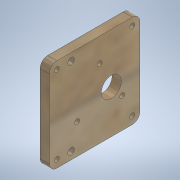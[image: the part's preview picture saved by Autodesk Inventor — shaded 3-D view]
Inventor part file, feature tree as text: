
AUTODESK INVENTOR PART (.ipt)
format: ipt  version: 2020.3 (Build 243373000, 373)  size: 305,664 bytes
history: native  units: mm
features: sketch x4, extrude x2, hole x2, other x1, fillet x1
ambient origin geometry x8: Origin, YZ Plane, XZ Plane, XY Plane, X Axis, Y Axis, Z Axis, Center Point
bodies: Body1 (feature_tree)
feature tree (10):
  other  "ソリッド1"
  extrude  "押し出し1"  Depth=55.5mm
  hole  "穴1"  [1 undecoded]
  hole  "穴2"  [1 undecoded]
  extrude  "押し出し3"  Depth=4.5mm
  fillet  "フィレット1"  Radius=4.5mm
  sketch  "スケッチ1"
  sketch  "スケッチ2"
  sketch  "スケッチ3"
  sketch  "スケッチ4"
note: 2 required parameter values undecoded (feature->parameter linkage not recoverable at this tier; creation-order binding heuristic only, values carry confidence <= 0.55)
